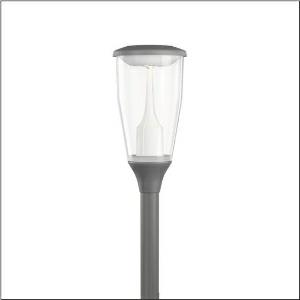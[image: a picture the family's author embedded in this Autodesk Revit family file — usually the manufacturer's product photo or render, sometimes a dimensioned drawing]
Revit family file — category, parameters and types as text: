
# Revit family: dl_11_iq___st1_2a_5xa5575kf14h000022_bb26
name_source: partatom
category: Lighting Fixtures
units: mm (PartAtom-declared; Revit-internal decimal feet)

## family parameters
Cut with Voids When Loaded = No
Host = Face
Light Source = No
Part Type = Normal
Room Calculation Point = No
Round Connector Dimension = Use Diameter
Shared = No

## types (1)
- --- (1 x LED, 1560 lm, 10 W, 4000K)
    Apparent Load = 10 VA
    CIE Flux Codes = 24 63 94 96 100
    Color Rendering = 70
    Color Temperature = 4000K
    Default Elevation = 1800 mm
    Description = DL 11 iQ, mast luminaire, Module 540 iQ-SR, primary light control with 3 zone facetted reflector, of plastic, silver coated, highly specular, structured, primary optical cover: cover, of PMMA, transparent, light distribution: ST1.2a, light emission: direct distribution, primary light characteristic: asymmetric, installation type: post-top, LED, High Power LED, light colour: 740, colour temperature: 4000K, control gear: iQ Street-Remote, control: Street-Remote, Auto-Match, Temp-Guard, Lumen-Switch, Night-Set, Smart-Wire, Light-Fading, Desk-Remote (wireless, voltage-free reading and setting of iQ features in the workshop via application-optimized NFC function/RFID function), optimised constant luminous flux control (CLO 2.0), mains connection: 220..240V, AC, 50/60Hz, connection cable pre-assembled, cable length: 5,5m, start of lifetime: 10W, end of service life: 10W, luminaire housing, upper part, of diecast aluminium, coated, SITECO metallic grey (DB 702S), spigot size: 76mm (post-top), mounting height: 3..5m, post-top mast mounting element, of diecast aluminium, coated, SITECO metallic grey (DB 702S), Module 540 iQ-SR, traffic white (RAL 9016), equipment: standard, protection rating (complete): IP66, insulation class (complete): insulation class II (safety insulation), certification: CE, ENEC, ENEC+, VDE, impact resistance: IK07, packaging unit: 1 piece

Light Distribution: ST1.2a
    Height = 665 mm
    Lamp = 1 x LED
    Lamp Light Flux = 1560 lm
    Lamp Power = 10 W
    Lamp count = 1
    Length = 334 mm
    Luminous efficacy = 156 lm/W
    Manufacturer = Siteco
    ModVariant = No
    Model = 5XA5575KF14H000022
    Number of Poles = 1
    OnlyDefault = Yes
    Power Factor = 1
    Product Name = DL 11 iQ | ST1.2a
    Product group = mast luminaire | pylon top
    ProductGroupID = 6100
    Protection Class = Protection class II
    Protection Degree = IP 66
    RLX_Detail_Level = 1
    RLX_Emergency_Light_Flux = 0 lm
    RLX_Emergency_Type = 0
    RLX_Emergency_Type_DB = No
    RlxData = <blob elided: 157173 chars, md5=c5d96656>
    Socket = socket
    Standby Power = 0 W
    System Light Flux = 1560 lm
    System Power = 10 W
    Type Comments = factory setting: luminous flux: 100 % | dim-lin: 254 | 401 mA
    Type Image = l_1258354.jpg
    URL = http://relux.com
    VarID = @adj_098791
    Voltage = 0 V
    Weight = 0.00 kg
    Width = 0 mm  [stored 0 ft]

note: [stored X ft] marks values corroborated as IEEE doubles in the binary element streams (Revit-internal decimal feet)

## geometry (parser evidence)
native form markers: Blend x4, Sweep x10
no freeform markers — native parametric forms only
